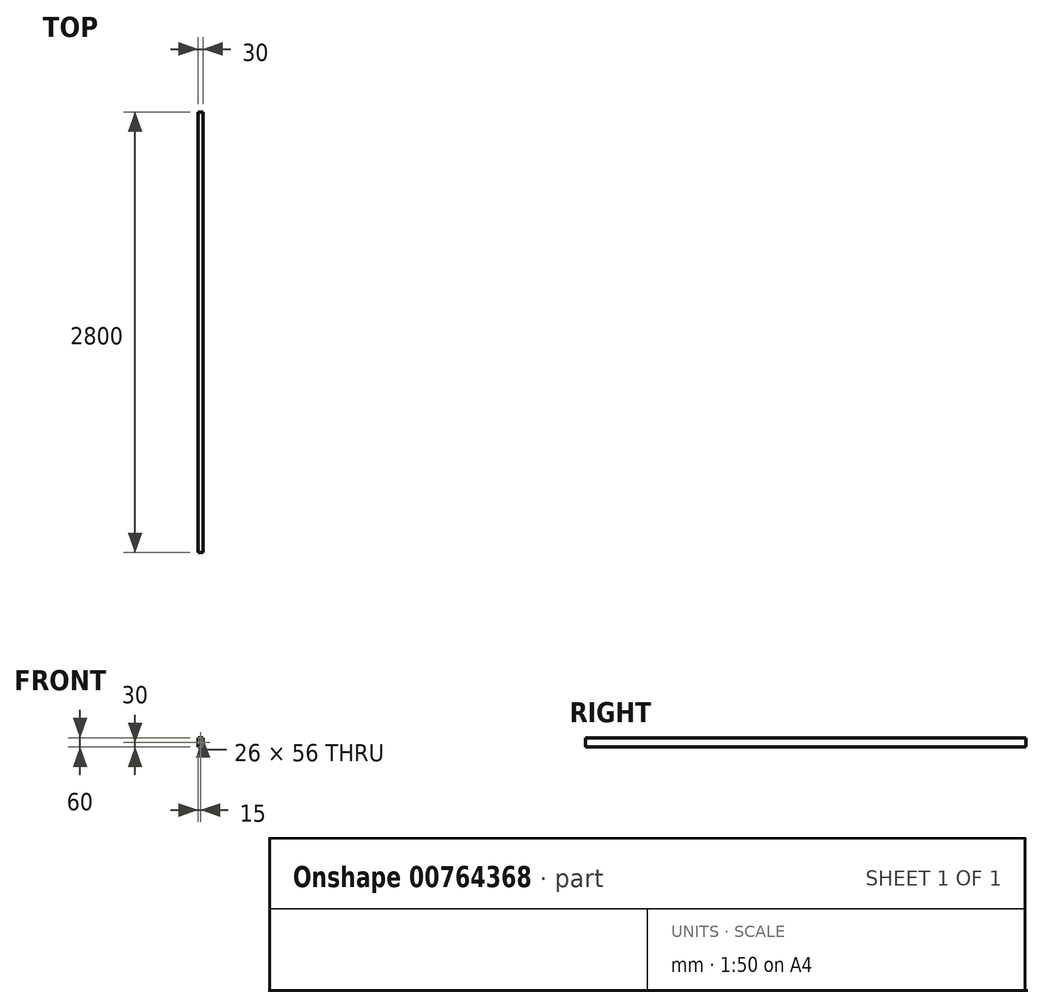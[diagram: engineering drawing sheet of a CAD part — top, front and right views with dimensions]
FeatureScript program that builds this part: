
annotation { "Feature Type Name" : "Feature", "Feature Type Description" : "" }
export const myFeature = defineFeature(function(context is Context, id is Id, definition is map)
    precondition{}
    {
        {
            var Q0;
            Q0=qCreatedBy(makeId("Front.planeOp"),FACE);
            var sketch = newSketch(context, id + "F0", { "sketchPlane" : qUnion([Q0])});
            skLineSegment(sketch, "E0", {"start": v(-15, 0) * mm, "end": v(-15, 30) * mm});
            skLineSegment(sketch, "E1", {"start": v(-15, 30) * mm, "end": v(15, 30) * mm});
            skLineSegment(sketch, "E2", {"start": v(15, 30) * mm, "end": v(15, -30) * mm});
            skLineSegment(sketch, "E3", {"start": v(15, -30) * mm, "end": v(-15, -30) * mm});
            skLineSegment(sketch, "E4", {"start": v(-15, -30) * mm, "end": v(-15, 0) * mm});
            skLineSegment(sketch, "E5.0", {"start": v(-13, 28) * mm, "end": v(13, 28) * mm});
            skLineSegment(sketch, "E5.1", {"start": v(-13, 0) * mm, "end": v(-13, 28) * mm});
            skLineSegment(sketch, "E5.2", {"start": v(13, 28) * mm, "end": v(13, -28) * mm});
            skLineSegment(sketch, "E5.3", {"start": v(13, -28) * mm, "end": v(-13, -28) * mm});
            skLineSegment(sketch, "E5.4", {"start": v(-13, -28) * mm, "end": v(-13, 0) * mm});
            skSolve(sketch);
        }
        {
            var Q0;
            Q0=makeQuery(id+"F0.imprint","IMPRINT",FACE,{"disambiguationData":[TD([[makeQuery(id+"F0.imprint","IMPRINT",EDGE,{"derivedFrom":sQuery(id+"F0.wireOp",EDGE,"E0")}),-1.0]])]});
            extrude(context, id + "F1", {"entities" : qUnion([Q0]), "depth" : 2800 * mm, "offsetDistance" : 25 * mm, "symmetric" : true});
        }
    });
